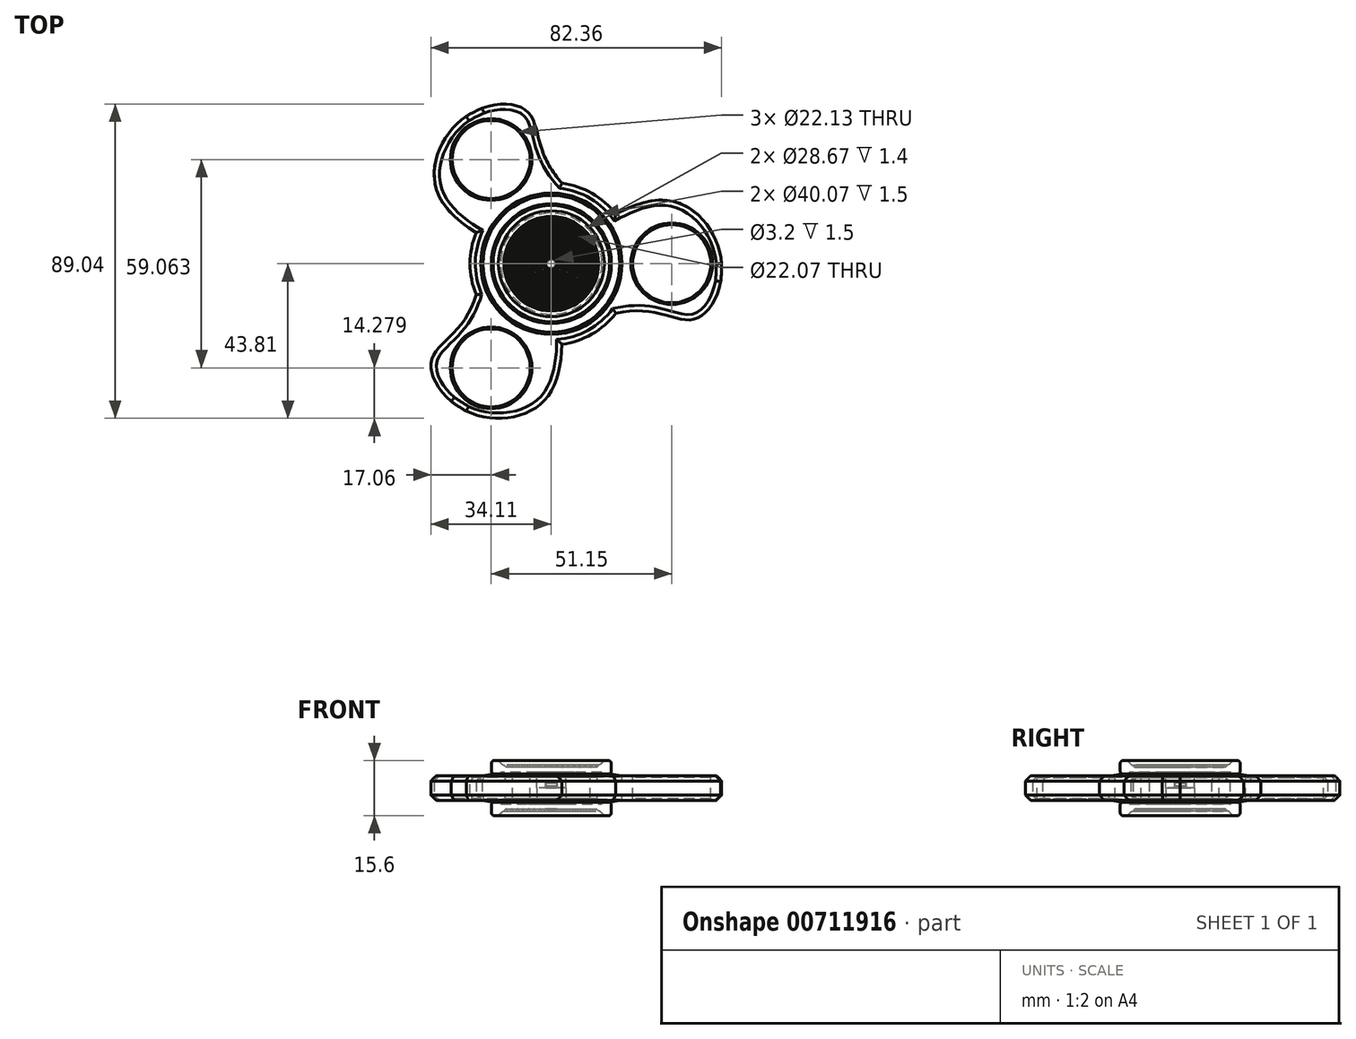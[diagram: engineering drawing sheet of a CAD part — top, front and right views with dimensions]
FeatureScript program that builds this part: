
annotation { "Feature Type Name" : "Feature", "Feature Type Description" : "" }
export const myFeature = defineFeature(function(context is Context, id is Id, definition is map)
    precondition{}
    {
        {
            var Q0;
            Q0=qCreatedBy(makeId("Front.planeOp"),FACE);
            var sketch = newSketch(context, id + "F0", { "sketchPlane" : qUnion([Q0])});
            skLineSegment(sketch, "E0", {"start": v(0, 0) * mm, "end": v(0, 3.5) * mm});
            skLineSegment(sketch, "E1", {"start": v(0, 3.5) * mm, "end": v(13.04, 3.5) * mm});
            skLineSegment(sketch, "E2", {"start": v(13.04, 3.5) * mm, "end": v(13.04, 2) * mm});
            skLineSegment(sketch, "E3", {"start": v(13.04, 2) * mm, "end": v(20.04, 2) * mm});
            skLineSegment(sketch, "E4", {"start": v(20.04, 2) * mm, "end": v(20.04, 3.5) * mm});
            skLineSegment(sketch, "E5", {"start": v(20.04, 3.5) * mm, "end": v(23.04, 3.5) * mm});
            skLineSegment(sketch, "E6", {"start": v(23.04, 3.5) * mm, "end": v(23.04, 0) * mm});
            skLineSegment(sketch, "E7", {"start": v(23.04, 0) * mm, "end": v(45.16, 0) * mm});
            skLineSegment(sketch, "E8", {"start": v(45.16, 0) * mm, "end": v(45.16, 3.5) * mm});
            skLineSegment(sketch, "E9", {"start": v(45.16, 3.5) * mm, "end": v(47.16, 3.5) * mm});
            skLineSegment(sketch, "E10", {"start": v(47.16, 3.5) * mm, "end": v(48.16, 1.5) * mm});
            skLineSegment(sketch, "E11", {"start": v(48.16, 1.5) * mm, "end": v(48.16, 0) * mm});
            skLineSegment(sketch, "E12", {"start": v(48.16, 0) * mm, "end": v(45.16, 0) * mm});
            skLineSegment(sketch, "E13", {"start": v(23.04, 0) * mm, "end": v(11.04, 0) * mm});
            skLineSegment(sketch, "E14", {"start": v(11.04, 0) * mm, "end": v(11.04, 3.5) * mm});
            skLineSegment(sketch, "E15", {"start": v(23.04, 3.5) * mm, "end": v(45.16, 3.5) * mm});
            skLineSegment(sketch, "E16", {"start": v(34.1, 0) * mm, "end": v(34.1, 3.5) * mm});
            skLineSegment(sketch, "E17", {"start": v(17, 4.5) * mm, "end": v(17, 6.5) * mm});
            skLineSegment(sketch, "E18", {"start": v(17, 6.5) * mm, "end": v(0, 6.5) * mm});
            skLineSegment(sketch, "E19", {"start": v(0, 6.5) * mm, "end": v(0, 0) * mm});
            skLineSegment(sketch, "E20", {"start": v(0, 0) * mm, "end": v(4.08, 0) * mm});
            skLineSegment(sketch, "E21", {"start": v(4.08, 0) * mm, "end": v(4.08, 3.5) * mm});
            skLineSegment(sketch, "E22", {"start": v(4.08, 3.5) * mm, "end": v(6.58, 3.5) * mm});
            skLineSegment(sketch, "E23", {"start": v(6.58, 3.5) * mm, "end": v(6.58, 4.5) * mm});
            skLineSegment(sketch, "E24", {"start": v(6.58, 4.5) * mm, "end": v(17, 4.5) * mm});
            skLineSegment(sketch, "E25", {"start": v(17, 6.5) * mm, "end": v(17, 7.8) * mm});
            skLineSegment(sketch, "E26", {"start": v(17, 7.8) * mm, "end": v(15, 7.8) * mm});
            skLineSegment(sketch, "E27", {"start": v(15, 7.8) * mm, "end": v(13.7, 6.5) * mm});
            skLineSegment(sketch, "E28.MirrorCS", {"start": v(13.04, -3.5) * mm, "end": v(13.04, -2) * mm});
            skLineSegment(sketch, "E29.MirrorCS", {"start": v(4.08, -3.5) * mm, "end": v(6.58, -3.5) * mm});
            skLineSegment(sketch, "E30.MirrorCS", {"start": v(20.04, -3.5) * mm, "end": v(23.04, -3.5) * mm});
            skLineSegment(sketch, "E31.MirrorCS", {"start": v(20.04, -2) * mm, "end": v(20.04, -3.5) * mm});
            skLineSegment(sketch, "E32.MirrorCS", {"start": v(47.16, -3.5) * mm, "end": v(48.16, -1.5) * mm});
            skLineSegment(sketch, "E33.MirrorCS", {"start": v(45.16, -3.5) * mm, "end": v(47.16, -3.5) * mm});
            skLineSegment(sketch, "E34.MirrorCS", {"start": v(0, -3.5) * mm, "end": v(13.04, -3.5) * mm});
            skLineSegment(sketch, "E35.MirrorCS", {"start": v(23.04, -3.5) * mm, "end": v(45.16, -3.5) * mm});
            skLineSegment(sketch, "E36.MirrorCS", {"start": v(13.04, -2) * mm, "end": v(20.04, -2) * mm});
            skLineSegment(sketch, "E37.MirrorCS", {"start": v(48.16, -1.5) * mm, "end": v(48.16, 0) * mm});
            skLineSegment(sketch, "E38.MirrorCS", {"start": v(45.16, 0) * mm, "end": v(45.16, -3.5) * mm});
            skLineSegment(sketch, "E39.MirrorCS", {"start": v(34.1, 0) * mm, "end": v(34.1, -3.5) * mm});
            skLineSegment(sketch, "E40.MirrorCS", {"start": v(23.04, -3.5) * mm, "end": v(23.04, 0) * mm});
            skLineSegment(sketch, "E41.MirrorCS", {"start": v(11.04, 0) * mm, "end": v(11.04, -3.5) * mm});
            skLineSegment(sketch, "E42.MirrorCS", {"start": v(4.08, 0) * mm, "end": v(4.08, -3.5) * mm});
            skLineSegment(sketch, "E43", {"start": v(1.6, 0) * mm, "end": v(1.6, 2) * mm});
            skLineSegment(sketch, "E44", {"start": v(1.6, 2) * mm, "end": v(0, 2) * mm});
            skLineSegment(sketch, "E45", {"start": v(14.34, 4.5) * mm, "end": v(14.34, 3.1) * mm});
            skLineSegment(sketch, "E46", {"start": v(14.34, 3.1) * mm, "end": v(19.38, 3.1) * mm});
            skLineSegment(sketch, "E47", {"start": v(19.38, 3.1) * mm, "end": v(19.38, 3.5) * mm});
            skLineSegment(sketch, "E48", {"start": v(19.38, 3.5) * mm, "end": v(16.5, 4) * mm});
            skLineSegment(sketch, "E49", {"start": v(16.5, 4) * mm, "end": v(17, 4.5) * mm});
            skLineSegment(sketch, "E50.MirrorCS", {"start": v(17, -4.5) * mm, "end": v(17, -6.5) * mm});
            skLineSegment(sketch, "E51.MirrorCS", {"start": v(17, -7.8) * mm, "end": v(15, -7.8) * mm});
            skLineSegment(sketch, "E52.MirrorCS", {"start": v(17, -6.5) * mm, "end": v(17, -7.8) * mm});
            skLineSegment(sketch, "E53.MirrorCS", {"start": v(17, -6.5) * mm, "end": v(0, -6.5) * mm});
            skLineSegment(sketch, "E54.MirrorCS", {"start": v(6.58, -4.5) * mm, "end": v(17, -4.5) * mm});
            skLineSegment(sketch, "E55.MirrorCS", {"start": v(15, -7.8) * mm, "end": v(13.7, -6.5) * mm});
            skLineSegment(sketch, "E56.MirrorCS", {"start": v(14.34, -3.1) * mm, "end": v(19.39, -3.1) * mm});
            skLineSegment(sketch, "E57.MirrorCS", {"start": v(19.39, -3.5) * mm, "end": v(16.5, -4) * mm});
            skLineSegment(sketch, "E58.MirrorCS", {"start": v(16.5, -4) * mm, "end": v(17, -4.5) * mm});
            skLineSegment(sketch, "E59.MirrorCS", {"start": v(14.34, -4.5) * mm, "end": v(14.34, -3.1) * mm});
            skLineSegment(sketch, "E60.MirrorCS", {"start": v(6.58, -3.5) * mm, "end": v(6.58, -4.5) * mm});
            skLineSegment(sketch, "E61.MirrorCS", {"start": v(0, -6.5) * mm, "end": v(0, 0) * mm});
            skLineSegment(sketch, "E62.MirrorCS", {"start": v(19.38, -3.1) * mm, "end": v(19.38, -3.5) * mm});
            skLineSegment(sketch, "E63", {"start": v(1, 6.5) * mm, "end": v(1.6, 5.9) * mm});
            skLineSegment(sketch, "E64", {"start": v(1.6, 5.9) * mm, "end": v(2.2, 6.5) * mm});
            skLineSegment(sketch, "E65.1.0.0", {"start": v(3.2, 5.9) * mm, "end": v(3.8, 6.5) * mm});
            skLineSegment(sketch, "E65.1.0.1", {"start": v(2.6, 6.5) * mm, "end": v(3.2, 5.9) * mm});
            skLineSegment(sketch, "E65.2.0.0", {"start": v(4.8, 5.9) * mm, "end": v(5.4, 6.5) * mm});
            skLineSegment(sketch, "E65.2.0.1", {"start": v(4.2, 6.5) * mm, "end": v(4.8, 5.9) * mm});
            skLineSegment(sketch, "E65.3.0.0", {"start": v(6.4, 5.9) * mm, "end": v(7, 6.5) * mm});
            skLineSegment(sketch, "E65.3.0.1", {"start": v(5.8, 6.5) * mm, "end": v(6.4, 5.9) * mm});
            skLineSegment(sketch, "E65.4.0.0", {"start": v(8, 5.9) * mm, "end": v(8.6, 6.5) * mm});
            skLineSegment(sketch, "E65.4.0.1", {"start": v(7.4, 6.5) * mm, "end": v(8, 5.9) * mm});
            skLineSegment(sketch, "E65.5.0.0", {"start": v(9.6, 5.9) * mm, "end": v(10.2, 6.5) * mm});
            skLineSegment(sketch, "E65.5.0.1", {"start": v(9, 6.5) * mm, "end": v(9.6, 5.9) * mm});
            skLineSegment(sketch, "E65.6.0.0", {"start": v(11.2, 5.9) * mm, "end": v(11.8, 6.5) * mm});
            skLineSegment(sketch, "E65.6.0.1", {"start": v(10.6, 6.5) * mm, "end": v(11.2, 5.9) * mm});
            skLineSegment(sketch, "E65.7.0.0", {"start": v(12.8, 5.9) * mm, "end": v(13.4, 6.5) * mm});
            skLineSegment(sketch, "E65.7.0.1", {"start": v(12.2, 6.5) * mm, "end": v(12.8, 5.9) * mm});
            skLineSegment(sketch, "E65.direction1", {"start": v(1.6, 5.9) * mm, "end": v(3.2, 5.9) * mm, "construction": true});
            skLineSegment(sketch, "E66.MirrorCS", {"start": v(1, -6.5) * mm, "end": v(1.6, -5.9) * mm});
            skLineSegment(sketch, "E67.MirrorCS", {"start": v(2.6, -6.5) * mm, "end": v(3.2, -5.9) * mm});
            skLineSegment(sketch, "E68.MirrorCS", {"start": v(1.6, -5.9) * mm, "end": v(2.2, -6.5) * mm});
            skLineSegment(sketch, "E69.MirrorCS", {"start": v(8, -5.9) * mm, "end": v(8.6, -6.5) * mm});
            skLineSegment(sketch, "E70.MirrorCS", {"start": v(9.6, -5.9) * mm, "end": v(10.2, -6.5) * mm});
            skLineSegment(sketch, "E71.MirrorCS", {"start": v(7.4, -6.5) * mm, "end": v(8, -5.9) * mm});
            skLineSegment(sketch, "E72.MirrorCS", {"start": v(10.6, -6.5) * mm, "end": v(11.2, -5.9) * mm});
            skLineSegment(sketch, "E73.MirrorCS", {"start": v(12.2, -6.5) * mm, "end": v(12.8, -5.9) * mm});
            skLineSegment(sketch, "E74.MirrorCS", {"start": v(6.4, -5.9) * mm, "end": v(7, -6.5) * mm});
            skLineSegment(sketch, "E75.MirrorCS", {"start": v(1.6, -5.9) * mm, "end": v(3.2, -5.9) * mm, "construction": true});
            skLineSegment(sketch, "E76.MirrorCS", {"start": v(11.2, -5.9) * mm, "end": v(11.8, -6.5) * mm});
            skLineSegment(sketch, "E77.MirrorCS", {"start": v(3.2, -5.9) * mm, "end": v(3.8, -6.5) * mm});
            skLineSegment(sketch, "E78.MirrorCS", {"start": v(12.8, -5.9) * mm, "end": v(13.4, -6.5) * mm});
            skLineSegment(sketch, "E79.MirrorCS", {"start": v(9, -6.5) * mm, "end": v(9.6, -5.9) * mm});
            skLineSegment(sketch, "E80.MirrorCS", {"start": v(4.8, -5.9) * mm, "end": v(5.4, -6.5) * mm});
            skLineSegment(sketch, "E81.MirrorCS", {"start": v(5.8, -6.5) * mm, "end": v(6.4, -5.9) * mm});
            skLineSegment(sketch, "E82.MirrorCS", {"start": v(4.2, -6.5) * mm, "end": v(4.8, -5.9) * mm});
            skSolve(sketch);
        }
        {
            var Q0;
            {var subQ1=sQuery(id+"F0.wireOp",EDGE,"E2");Q0=makeQuery(id+"F0.imprint","IMPRINT",FACE,{"disambiguationData":[TD([[makeQuery(id+"F0.imprint","IMPRINT",EDGE,{"derivedFrom":subQ1}),-1.0]])]});}
            var Q1;
            Q1=makeQuery(id+"F0.imprint","IMPRINT",FACE,{"disambiguationData":[TD([[makeQuery(id+"F0.imprint","IMPRINT",EDGE,{"derivedFrom":sQuery(id+"F0.wireOp",EDGE,"E13")}),1.0]])]});
            var Q2;
            {var subQ0=sQuery(id+"F0.wireOp",EDGE,"E6");Q2=makeQuery(id+"F0.imprint","IMPRINT",FACE,{"disambiguationData":[TD([[makeQuery(id+"F0.imprint","IMPRINT",EDGE,{"derivedFrom":subQ0}),1.0]])]});}
            var Q3;
            {var subQ2=sQuery(id+"F0.wireOp",EDGE,"E39.MirrorCS");Q3=makeQuery(id+"F0.imprint","IMPRINT",FACE,{"disambiguationData":[TD([[makeQuery(id+"F0.imprint","IMPRINT",EDGE,{"derivedFrom":subQ2}),-1.0]])]});}
            var Q4;
            {var subQ0=sQuery(id+"F0.wireOp",EDGE,"E8");Q4=makeQuery(id+"F0.imprint","IMPRINT",FACE,{"disambiguationData":[TD([[makeQuery(id+"F0.imprint","IMPRINT",EDGE,{"derivedFrom":subQ0}),1.0]])]});}
            var Q5;
            {var subQ0=sQuery(id+"F0.wireOp",EDGE,"E38.MirrorCS");Q5=makeQuery(id+"F0.imprint","IMPRINT",FACE,{"disambiguationData":[TD([[makeQuery(id+"F0.imprint","IMPRINT",EDGE,{"derivedFrom":subQ0}),-1.0]])]});}
            var Q6;
            Q6=makeQuery(id+"F0.imprint","IMPRINT",FACE,{"disambiguationData":[TD([[makeQuery(id+"F0.imprint","IMPRINT",EDGE,{"derivedFrom":sQuery(id+"F0.wireOp",EDGE,"E8")}),-1.0]])]});
            var Q7;
            Q7=makeQuery(id+"F0.imprint","IMPRINT",FACE,{"disambiguationData":[TD([[makeQuery(id+"F0.imprint","IMPRINT",EDGE,{"derivedFrom":sQuery(id+"F0.wireOp",EDGE,"E12")}),1.0]])]});
            var Q8;
            Q8=sQuery(id+"F0.wireOp",EDGE,"E19");
            revolve(context, id + "F1", {"surfaceOperationType" : NewSurfaceOperationType.NEW, "entities" : qUnion([Q0, Q1, Q2, Q3, Q4, Q5, Q6, Q7]), "axis" : qUnion([Q8]), "revolveType" : RevolveType.FULL});
        }
        {
            var Q0;
            {var subQ0=sQuery(id+"F0.wireOp",EDGE,"E8");Q0=makeQuery(id+"F0.imprint","IMPRINT",FACE,{"disambiguationData":[TD([[makeQuery(id+"F0.imprint","IMPRINT",EDGE,{"derivedFrom":subQ0}),1.0]])]});}
            var Q1;
            {var subQ0=sQuery(id+"F0.wireOp",EDGE,"E38.MirrorCS");Q1=makeQuery(id+"F0.imprint","IMPRINT",FACE,{"disambiguationData":[TD([[makeQuery(id+"F0.imprint","IMPRINT",EDGE,{"derivedFrom":subQ0}),-1.0]])]});}
            var Q2;
            Q2=sQuery(id+"F0.wireOp",EDGE,"E39.MirrorCS");
            revolve(context, id + "F2", {"surfaceOperationType" : NewSurfaceOperationType.NEW, "entities" : qUnion([Q0, Q1]), "axis" : qUnion([Q2]), "revolveType" : RevolveType.FULL});
        }
        {
            var Q0;
            Q0=makeQuery(id+"F0.imprint","IMPRINT",FACE,{"disambiguationData":[TD([[makeQuery(id+"F0.imprint","IMPRINT",EDGE,{"derivedFrom":sQuery(id+"F0.wireOp",EDGE,"KGeZFjar-oYJH-GqHQ-ATJc-c8EllFN0LwBf")}),1.0]])]});
            var Q1;
            {var subQ0=sQuery(id+"F0.wireOp",EDGE,"E21");Q1=makeQuery(id+"F0.imprint","IMPRINT",FACE,{"disambiguationData":[TD([[makeQuery(id+"F0.imprint","IMPRINT",EDGE,{"derivedFrom":subQ0}),1.0]])]});}
            var Q2;
            {var subQ0=sQuery(id+"F0.wireOp",EDGE,"E25");Q2=makeQuery(id+"F0.imprint","IMPRINT",FACE,{"disambiguationData":[TD([[makeQuery(id+"F0.imprint","IMPRINT",EDGE,{"derivedFrom":subQ0}),1.0]])]});}
            var Q3;
            {var subQ1=sQuery(id+"F0.wireOp",EDGE,"E17");Q3=makeQuery(id+"F0.imprint","IMPRINT",FACE,{"disambiguationData":[TD([[makeQuery(id+"F0.imprint","IMPRINT",EDGE,{"derivedFrom":subQ1}),1.0]])]});}
            var Q4;
            {var subQ0=sQuery(id+"F0.wireOp",EDGE,"E45");Q4=makeQuery(id+"F0.imprint","IMPRINT",FACE,{"disambiguationData":[TD([[makeQuery(id+"F0.imprint","IMPRINT",EDGE,{"derivedFrom":subQ0}),1.0]])]});}
            var Q5;
            Q5=makeQuery(id+"F0.imprint","IMPRINT",FACE,{"disambiguationData":[TD([[makeQuery(id+"F0.imprint","IMPRINT",EDGE,{"derivedFrom":sQuery(id+"F0.wireOp",EDGE,"vZCheLl1-PAfG-MPR2-0KO7-rnN0XizPisMo.bottom")}),-1.0]])]});
            var Q6;
            Q6=sQuery(id+"F0.wireOp",EDGE,"E19");
            revolve(context, id + "F3", {"surfaceOperationType" : NewSurfaceOperationType.NEW, "entities" : qUnion([Q0, Q1, Q2, Q3, Q4, Q5]), "axis" : qUnion([Q6]), "revolveType" : RevolveType.FULL});
        }
        {
            var Q0;
            {var subQ0=sQuery(id+"F0.wireOp",EDGE,"E42.MirrorCS");Q0=makeQuery(id+"F0.imprint","IMPRINT",FACE,{"disambiguationData":[TD([[makeQuery(id+"F0.imprint","IMPRINT",EDGE,{"derivedFrom":subQ0}),-1.0]])]});}
            var Q1;
            {var subQ9=sQuery(id+"F0.wireOp",EDGE,"E50.MirrorCS");Q1=makeQuery(id+"F0.imprint","IMPRINT",FACE,{"disambiguationData":[TD([[makeQuery(id+"F0.imprint","IMPRINT",EDGE,{"derivedFrom":subQ9}),-1.0]])]});}
            var Q2;
            {var subQ0=sQuery(id+"F0.wireOp",EDGE,"3c67924d-497e-40e4-b348-fd03371842f01.MirrorCS");Q2=makeQuery(id+"F0.imprint","IMPRINT",FACE,{"disambiguationData":[TD([[makeQuery(id+"F0.imprint","IMPRINT",EDGE,{"derivedFrom":subQ0}),1.0]])]});}
            var Q3;
            Q3=makeQuery(id+"F0.imprint","IMPRINT",FACE,{"disambiguationData":[TD([[makeQuery(id+"F0.imprint","IMPRINT",EDGE,{"derivedFrom":sQuery(id+"F0.wireOp",EDGE,"E56.MirrorCS")}),-1.0]])]});
            var Q4;
            Q4=makeQuery(id+"F0.imprint","IMPRINT",FACE,{"disambiguationData":[TD([[makeQuery(id+"F0.imprint","IMPRINT",EDGE,{"derivedFrom":sQuery(id+"F0.wireOp",EDGE,"E51.MirrorCS")}),-1.0]])]});
            var Q5;
            {var subQ4=sQuery(id+"F0.wireOp",EDGE,"E43");Q5=makeQuery(id+"F0.imprint","IMPRINT",FACE,{"disambiguationData":[TD([[makeQuery(id+"F0.imprint","IMPRINT",EDGE,{"derivedFrom":subQ4}),1.0]])]});}
            var Q6;
            {var subQ3=sQuery(id+"F0.wireOp",EDGE,"E44");Q6=makeQuery(id+"F0.imprint","IMPRINT",FACE,{"disambiguationData":[TD([[makeQuery(id+"F0.imprint","IMPRINT",EDGE,{"derivedFrom":subQ3}),1.0]])]});}
            var Q7;
            Q7=sQuery(id+"F0.wireOp",EDGE,"E61.MirrorCS");
            revolve(context, id + "F4", {"surfaceOperationType" : NewSurfaceOperationType.NEW, "entities" : qUnion([Q0, Q1, Q2, Q3, Q4, Q5, Q6]), "axis" : qUnion([Q7]), "revolveType" : RevolveType.FULL});
        }
        {
            var Q0;
            Q0=makeQuery(id+"F2.opRevolve","SWEPT_BODY",BODY,{"disambiguationData":[OSD([sQuery(id+"F0.wireOp",EDGE,"E8"),sQuery(id+"F0.wireOp",EDGE,"E15"),sQuery(id+"F0.wireOp",EDGE,"E16"),sQuery(id+"F0.wireOp",EDGE,"E35.MirrorCS"),sQuery(id+"F0.wireOp",EDGE,"E38.MirrorCS"),sQuery(id+"F0.wireOp",EDGE,"E39.MirrorCS")])]});
            var Q1;
            Q1=makeQuery(id+"F1.opRevolve","SWEPT_EDGE",EDGE,{"disambiguationData":[OSD([sQuery(id+"F0.wireOp",EDGE,"E34.MirrorCS"),sQuery(id+"F0.wireOp",EDGE,"E41.MirrorCS")])]});
            circularPattern(context, id + "F5", {"entities" : qUnion([Q0]), "axis" : qUnion([Q1]), "angle" : 360 * degree, "instanceCount" : 3, "equalSpace" : true});
        }
        {
            var Q0;
            Q0=qCreatedBy(makeId("Top.planeOp"),FACE);
            var sketch = newSketch(context, id + "F6", { "sketchPlane" : qUnion([Q0])});
            skCircle(sketch, "E83", {"center": v(0, 0) * mm, "radius": 48.25 * mm});
            skFitSpline(sketch, "E84", {"points": [v(0, -25) * mm, v(27.25, -13.5) * mm, v(41.25, -15.5) * mm, v(48.25, 0) * mm, v(34, 17.78) * mm, v(0, 0) * mm], "startDerivative": vector(107.2, 120.6) * mm, "endDerivative": vector(-125.88, -120.18) * mm});
            skCircle(sketch, "E85", {"center": v(0, 0) * mm, "radius": 22.05 * mm});
            skSolve(sketch);
        }
        {
            var Q0;
            {var subQ0=sQuery(id+"F6.wireOp",EDGE,"E84");var subQ1=sQuery(id+"F6.wireOp",EDGE,"E83");var subQ2=makeQuery(id+"F6.imprint","INTERSECT",VERTEX,{"disambiguationData":[OD(0.0)],"derivedFrom":[subQ1,subQ0]});Q0=makeQuery(id+"F6.imprint","IMPRINT",FACE,{"disambiguationData":[TD([[makeQuery(id+"F6.imprint","IMPRINT",EDGE,{"disambiguationData":[TD([[subQ2,-1.0]])],"derivedFrom":subQ1}),1.0]])]});}
            extrude(context, id + "F7", {"entities" : qUnion([Q0]), "depth" : 3.5 * mm, "offsetDistance" : 25 * mm, "hasSecondDirection" : true, "secondDirectionOppositeDirection" : true, "secondDirectionDepth" : 3.5 * mm});
        }
        {
            var Q0;
            Q0=makeQuery(id+"F7.opExtrude","SWEPT_BODY",BODY,{"disambiguationData":[OSD([sQuery(id+"F6.wireOp",EDGE,"E83"),sQuery(id+"F6.wireOp",EDGE,"E84"),sQuery(id+"F6.wireOp",EDGE,"E85")])]});
            var Q1;
            Q1=makeQuery(id+"F1.opRevolve","SWEPT_FACE",FACE,{"disambiguationData":[OSD([sQuery(id+"F0.wireOp",EDGE,"E14"),sQuery(id+"F0.wireOp",EDGE,"E41.MirrorCS")])]});
            circularPattern(context, id + "F8", {"entities" : qUnion([Q0]), "axis" : qUnion([Q1]), "angle" : 360 * degree, "instanceCount" : 3, "equalSpace" : true});
        }
        {
            var Q0;
            {var subQ1=sQuery(id+"F0.wireOp",EDGE,"E2");Q0=makeQuery(id+"F0.imprint","IMPRINT",FACE,{"disambiguationData":[TD([[makeQuery(id+"F0.imprint","IMPRINT",EDGE,{"derivedFrom":subQ1}),-1.0]])]});}
            var Q1;
            Q1=makeQuery(id+"F0.imprint","IMPRINT",FACE,{"disambiguationData":[TD([[makeQuery(id+"F0.imprint","IMPRINT",EDGE,{"derivedFrom":sQuery(id+"F0.wireOp",EDGE,"E13")}),1.0]])]});
            var Q2;
            Q2=sQuery(id+"F0.wireOp",EDGE,"E19");
            revolve(context, id + "F9", {"surfaceOperationType" : NewSurfaceOperationType.NEW, "entities" : qUnion([Q0, Q1]), "axis" : qUnion([Q2]), "revolveType" : RevolveType.FULL});
        }
        {
            var Q0;
            Q0=makeQuery(id+"F8.opPattern","COPY",BODY,{"derivedFrom":makeQuery(id+"F7.opExtrude","SWEPT_BODY",BODY,{"disambiguationData":[OSD([sQuery(id+"F6.wireOp",EDGE,"E83"),sQuery(id+"F6.wireOp",EDGE,"E84"),sQuery(id+"F6.wireOp",EDGE,"E85")])]}),"instanceName":"2"});
            var Q1;
            Q1=makeQuery(id+"F8.opPattern","COPY",BODY,{"derivedFrom":makeQuery(id+"F7.opExtrude","SWEPT_BODY",BODY,{"disambiguationData":[OSD([sQuery(id+"F6.wireOp",EDGE,"E83"),sQuery(id+"F6.wireOp",EDGE,"E84"),sQuery(id+"F6.wireOp",EDGE,"E85")])]}),"instanceName":"1"});
            var Q2;
            Q2=makeQuery(id+"F7.opExtrude","SWEPT_BODY",BODY,{"disambiguationData":[OSD([sQuery(id+"F6.wireOp",EDGE,"E83"),sQuery(id+"F6.wireOp",EDGE,"E84"),sQuery(id+"F6.wireOp",EDGE,"E85")])]});
            var Q3;
            Q3=makeQuery(id+"F9.opRevolve","SWEPT_BODY",BODY,{"disambiguationData":[OSD([sQuery(id+"F0.wireOp",EDGE,"E1"),sQuery(id+"F0.wireOp",EDGE,"E2"),sQuery(id+"F0.wireOp",EDGE,"E3"),sQuery(id+"F0.wireOp",EDGE,"E4"),sQuery(id+"F0.wireOp",EDGE,"E5"),sQuery(id+"F0.wireOp",EDGE,"E6"),sQuery(id+"F0.wireOp",EDGE,"E19"),sQuery(id+"F0.wireOp",EDGE,"E22"),sQuery(id+"F0.wireOp",EDGE,"E28.MirrorCS"),sQuery(id+"F0.wireOp",EDGE,"E30.MirrorCS"),sQuery(id+"F0.wireOp",EDGE,"E31.MirrorCS"),sQuery(id+"F0.wireOp",EDGE,"E34.MirrorCS"),sQuery(id+"F0.wireOp",EDGE,"E36.MirrorCS"),sQuery(id+"F0.wireOp",EDGE,"E40.MirrorCS"),sQuery(id+"F0.wireOp",EDGE,"05ecb766-ba4e-4d32-9f54-2b1253087cd20.MirrorCS")])]});
            booleanBodies(context, id + "F10", {"operationType" : BooleanOperationType.UNION, "tools" : qUnion([Q0, Q1, Q2, Q3])});
        }
        {
            var Q0;
            Q0=makeQuery(id+"F1.opRevolve","SWEPT_BODY",BODY,{"disambiguationData":[OSD([sQuery(id+"F0.wireOp",EDGE,"E1"),sQuery(id+"F0.wireOp",EDGE,"E2"),sQuery(id+"F0.wireOp",EDGE,"E3"),sQuery(id+"F0.wireOp",EDGE,"E4"),sQuery(id+"F0.wireOp",EDGE,"E5"),sQuery(id+"F0.wireOp",EDGE,"E9"),sQuery(id+"F0.wireOp",EDGE,"E10"),sQuery(id+"F0.wireOp",EDGE,"E11"),sQuery(id+"F0.wireOp",EDGE,"E14"),sQuery(id+"F0.wireOp",EDGE,"E15"),sQuery(id+"F0.wireOp",EDGE,"E28.MirrorCS"),sQuery(id+"F0.wireOp",EDGE,"E30.MirrorCS"),sQuery(id+"F0.wireOp",EDGE,"E31.MirrorCS"),sQuery(id+"F0.wireOp",EDGE,"E32.MirrorCS"),sQuery(id+"F0.wireOp",EDGE,"E33.MirrorCS"),sQuery(id+"F0.wireOp",EDGE,"E34.MirrorCS"),sQuery(id+"F0.wireOp",EDGE,"E35.MirrorCS"),sQuery(id+"F0.wireOp",EDGE,"E36.MirrorCS"),sQuery(id+"F0.wireOp",EDGE,"E37.MirrorCS"),sQuery(id+"F0.wireOp",EDGE,"E41.MirrorCS")])]});
            deleteBodies(context, id + "F11", {"entities" : qUnion([Q0])});
        }
        {
            var Q0;
            Q0=makeQuery(id+"F5.opPattern","COPY",BODY,{"derivedFrom":makeQuery(id+"F2.opRevolve","SWEPT_BODY",BODY,{"disambiguationData":[OSD([sQuery(id+"F0.wireOp",EDGE,"E8"),sQuery(id+"F0.wireOp",EDGE,"E15"),sQuery(id+"F0.wireOp",EDGE,"E16"),sQuery(id+"F0.wireOp",EDGE,"E35.MirrorCS"),sQuery(id+"F0.wireOp",EDGE,"E38.MirrorCS"),sQuery(id+"F0.wireOp",EDGE,"E39.MirrorCS")])]}),"instanceName":"2"});
            var Q1;
            Q1=makeQuery(id+"F5.opPattern","COPY",BODY,{"derivedFrom":makeQuery(id+"F2.opRevolve","SWEPT_BODY",BODY,{"disambiguationData":[OSD([sQuery(id+"F0.wireOp",EDGE,"E8"),sQuery(id+"F0.wireOp",EDGE,"E15"),sQuery(id+"F0.wireOp",EDGE,"E16"),sQuery(id+"F0.wireOp",EDGE,"E35.MirrorCS"),sQuery(id+"F0.wireOp",EDGE,"E38.MirrorCS"),sQuery(id+"F0.wireOp",EDGE,"E39.MirrorCS")])]}),"instanceName":"1"});
            var Q2;
            Q2=makeQuery(id+"F2.opRevolve","SWEPT_BODY",BODY,{"disambiguationData":[OSD([sQuery(id+"F0.wireOp",EDGE,"E8"),sQuery(id+"F0.wireOp",EDGE,"E15"),sQuery(id+"F0.wireOp",EDGE,"E16"),sQuery(id+"F0.wireOp",EDGE,"E35.MirrorCS"),sQuery(id+"F0.wireOp",EDGE,"E38.MirrorCS"),sQuery(id+"F0.wireOp",EDGE,"E39.MirrorCS")])]});
            var Q3;
            Q3=makeQuery(id+"F8.opPattern","COPY",BODY,{"derivedFrom":makeQuery(id+"F7.opExtrude","SWEPT_BODY",BODY,{"disambiguationData":[OSD([sQuery(id+"F6.wireOp",EDGE,"E83"),sQuery(id+"F6.wireOp",EDGE,"E84"),sQuery(id+"F6.wireOp",EDGE,"E85")])]}),"instanceName":"2"});
            booleanBodies(context, id + "F12", {"operationType" : BooleanOperationType.SUBTRACTION, "tools" : qUnion([Q0, Q1, Q2]), "targets" : qUnion([Q3])});
        }
        {
            var Q0;
            Q0=makeQuery(id+"F9.opRevolve","SWEPT_EDGE",EDGE,{"disambiguationData":[OSD([sQuery(id+"F0.wireOp",EDGE,"E28.MirrorCS"),sQuery(id+"F0.wireOp",EDGE,"E34.MirrorCS")])]});
            var Q1;
            Q1=makeQuery(id+"F9.opRevolve","SWEPT_EDGE",EDGE,{"disambiguationData":[OSD([sQuery(id+"F0.wireOp",EDGE,"E34.MirrorCS"),sQuery(id+"F0.wireOp",EDGE,"E41.MirrorCS")])]});
            var Q2;
            Q2=makeQuery(id+"F12.opBoolean","COPY",FACE,{"derivedFrom":makeQuery(id+"F5.opPattern","COPY",FACE,{"derivedFrom":makeQuery(id+"F2.opRevolve","SWEPT_FACE",FACE,{"disambiguationData":[OSD([sQuery(id+"F0.wireOp",EDGE,"E8"),sQuery(id+"F0.wireOp",EDGE,"E38.MirrorCS")])]}),"instanceName":"1"})});
            var Q3;
            Q3=makeQuery(id+"F12.opBoolean","COPY",FACE,{"derivedFrom":makeQuery(id+"F5.opPattern","COPY",FACE,{"derivedFrom":makeQuery(id+"F2.opRevolve","SWEPT_FACE",FACE,{"disambiguationData":[OSD([sQuery(id+"F0.wireOp",EDGE,"E8"),sQuery(id+"F0.wireOp",EDGE,"E38.MirrorCS")])]}),"instanceName":"2"})});
            var Q4;
            Q4=makeQuery(id+"F12.opBoolean","COPY",FACE,{"derivedFrom":makeQuery(id+"F2.opRevolve","SWEPT_FACE",FACE,{"disambiguationData":[OSD([sQuery(id+"F0.wireOp",EDGE,"E8"),sQuery(id+"F0.wireOp",EDGE,"E38.MirrorCS")])]})});
            var Q5;
            Q5=makeQuery(id+"F9.opRevolve","SWEPT_FACE",FACE,{"disambiguationData":[OSD([sQuery(id+"F0.wireOp",EDGE,"E1")])]});
            var Q6;
            Q6=makeQuery(id+"F4.opRevolve","SWEPT_EDGE",EDGE,{"disambiguationData":[OSD([sQuery(id+"F0.wireOp",EDGE,"E43"),sQuery(id+"F0.wireOp",EDGE,"E44")])]});
            var Q7;
            Q7=makeQuery(id+"F4.opRevolve","SWEPT_EDGE",EDGE,{"disambiguationData":[OSD([sQuery(id+"F0.wireOp",EDGE,"b50aee2d-b4f1-476f-93b3-e66e5736d9cd34.MirrorCS"),sQuery(id+"F0.wireOp",EDGE,"b50aee2d-b4f1-476f-93b3-e66e5736d9cd41.MirrorCS")])]});
            var Q8;
            Q8=makeQuery(id+"F4.opRevolve","SWEPT_EDGE",EDGE,{"disambiguationData":[OSD([sQuery(id+"F0.wireOp",EDGE,"b50aee2d-b4f1-476f-93b3-e66e5736d9cd12.MirrorCS"),sQuery(id+"F0.wireOp",EDGE,"b50aee2d-b4f1-476f-93b3-e66e5736d9cd41.MirrorCS")])]});
            var Q9;
            Q9=makeQuery(id+"F3.opRevolve","SWEPT_EDGE",EDGE,{"disambiguationData":[OSD([sQuery(id+"F0.wireOp",EDGE,"E20"),sQuery(id+"F0.wireOp",EDGE,"E43")])]});
            var Q10;
            Q10=makeQuery(id+"F3.opRevolve","SWEPT_EDGE",EDGE,{"disambiguationData":[OSD([sQuery(id+"F0.wireOp",EDGE,"KGeZFjar-oYJH-GqHQ-ATJc-c8EllFN0LwBf"),sQuery(id+"F0.wireOp",EDGE,"cmr94KfM-78bh-h436-o3Y6-E5B6DGNtIqfJ")])]});
            var Q11;
            Q11=makeQuery(id+"F3.opRevolve","SWEPT_EDGE",EDGE,{"disambiguationData":[OSD([sQuery(id+"F0.wireOp",EDGE,"cmr94KfM-78bh-h436-o3Y6-E5B6DGNtIqfJ"),sQuery(id+"F0.wireOp",EDGE,"ut3q9B5h-MosH-EnmA-Wy3q-ChUi5hh3IWyW")])]});
            var Q12;
            Q12=makeQuery(id+"F3.opRevolve","SWEPT_EDGE",EDGE,{"disambiguationData":[OSD([sQuery(id+"F0.wireOp",EDGE,"E25"),sQuery(id+"F0.wireOp",EDGE,"E26")])]});
            var Q13;
            Q13=makeQuery(id+"F4.opRevolve","SWEPT_EDGE",EDGE,{"disambiguationData":[OSD([sQuery(id+"F0.wireOp",EDGE,"E51.MirrorCS"),sQuery(id+"F0.wireOp",EDGE,"E52.MirrorCS")])]});
            var Q14;
            Q14=makeQuery(id+"F4.opRevolve","SWEPT_EDGE",EDGE,{"disambiguationData":[OSD([sQuery(id+"F0.wireOp",EDGE,"E44"),sQuery(id+"F0.wireOp",EDGE,"E43")])]});
            chamfer(context, id + "F13", {"entities" : qUnion([Q0, Q1, Q2, Q3, Q4, Q5, Q6, Q7, Q8, Q9, Q10, Q11, Q12, Q13, Q14]), "width" : 0.5 * mm, "tangentPropagation" : true});
        }
        {
            var Q0;
            {var subQ0=sQuery(id+"F6.wireOp",EDGE,"E84");Q0=makeQuery(id+"F8.opPattern","COPY",EDGE,{"derivedFrom":makeQuery(id+"F7.opExtrude","CAP_EDGE",EDGE,{"disambiguationData":[OSD([subQ0]),TDD([makeQuery(id+"F6.imprint","IMPRINT",EDGE,{"disambiguationData":[TD([[makeQuery(id+"F6.imprint","INTERSECT",VERTEX,{"disambiguationData":[OD(1.0)],"derivedFrom":[sQuery(id+"F6.wireOp",EDGE,"E83"),subQ0]}),-1.0]])],"derivedFrom":subQ0})])],"isStart":false}),"instanceName":"1"});}
            var Q1;
            {var subQ0=sQuery(id+"F6.wireOp",EDGE,"E84");var subQ1=sQuery(id+"F6.wireOp",EDGE,"E83");var subQ4=sQuery(id+"F0.wireOp",EDGE,"E6");var subQ5=sQuery(id+"F0.wireOp",EDGE,"E5");Q1=makeQuery(id+"F10.opBoolean","SPLIT",EDGE,{"disambiguationData":[TD([makeQuery(id+"F7.opExtrude","SWEPT_FACE",FACE,{"disambiguationData":[OSD([subQ0]),TDD([makeQuery(id+"F6.imprint","IMPRINT",EDGE,{"disambiguationData":[TD([[makeQuery(id+"F6.imprint","INTERSECT",VERTEX,{"disambiguationData":[OD(0.0)],"derivedFrom":[subQ1,subQ0]}),1.0]])],"derivedFrom":subQ0})])]})])],"derivedFrom":makeQuery(id+"F9.opRevolve","SWEPT_EDGE",EDGE,{"disambiguationData":[OSD([subQ5,subQ4,sQuery(id+"F0.wireOp",EDGE,"E15")])]})});}
            var Q2;
            Q2=makeQuery(id+"F8.opPattern","COPY",EDGE,{"derivedFrom":makeQuery(id+"F7.opExtrude","CAP_EDGE",EDGE,{"disambiguationData":[OSD([sQuery(id+"F6.wireOp",EDGE,"E83")])],"isStart":false}),"instanceName":"1"});
            var Q3;
            {var subQ0=sQuery(id+"F6.wireOp",EDGE,"E84");Q3=makeQuery(id+"F8.opPattern","COPY",EDGE,{"derivedFrom":makeQuery(id+"F7.opExtrude","CAP_EDGE",EDGE,{"disambiguationData":[OSD([subQ0]),TDD([makeQuery(id+"F6.imprint","IMPRINT",EDGE,{"disambiguationData":[TD([[makeQuery(id+"F6.imprint","INTERSECT",VERTEX,{"disambiguationData":[OD(0.0)],"derivedFrom":[sQuery(id+"F6.wireOp",EDGE,"E83"),subQ0]}),1.0]])],"derivedFrom":subQ0})])],"isStart":false}),"instanceName":"1"});}
            var Q4;
            {var subQ1=sQuery(id+"F6.wireOp",EDGE,"E84");var subQ2=sQuery(id+"F6.wireOp",EDGE,"E83");var subQ4=sQuery(id+"F0.wireOp",EDGE,"E5");var subQ5=sQuery(id+"F0.wireOp",EDGE,"E6");Q4=makeQuery(id+"F10.opBoolean","SPLIT",EDGE,{"disambiguationData":[TD([makeQuery(id+"F8.opPattern","COPY",FACE,{"derivedFrom":makeQuery(id+"F7.opExtrude","SWEPT_FACE",FACE,{"disambiguationData":[OSD([subQ1]),TDD([makeQuery(id+"F6.imprint","IMPRINT",EDGE,{"disambiguationData":[TD([[makeQuery(id+"F6.imprint","INTERSECT",VERTEX,{"disambiguationData":[OD(0.0)],"derivedFrom":[subQ2,subQ1]}),1.0]])],"derivedFrom":subQ1})])]}),"instanceName":"1"})])],"derivedFrom":makeQuery(id+"F9.opRevolve","SWEPT_EDGE",EDGE,{"disambiguationData":[OSD([subQ4,subQ5,sQuery(id+"F0.wireOp",EDGE,"E15")])]})});}
            var Q5;
            {var subQ0=sQuery(id+"F6.wireOp",EDGE,"E84");Q5=makeQuery(id+"F8.opPattern","COPY",EDGE,{"derivedFrom":makeQuery(id+"F7.opExtrude","CAP_EDGE",EDGE,{"disambiguationData":[OSD([subQ0]),TDD([makeQuery(id+"F6.imprint","IMPRINT",EDGE,{"disambiguationData":[TD([[makeQuery(id+"F6.imprint","INTERSECT",VERTEX,{"disambiguationData":[OD(1.0)],"derivedFrom":[sQuery(id+"F6.wireOp",EDGE,"E83"),subQ0]}),-1.0]])],"derivedFrom":subQ0})])],"isStart":false}),"instanceName":"2"});}
            var Q6;
            Q6=makeQuery(id+"F8.opPattern","COPY",EDGE,{"derivedFrom":makeQuery(id+"F7.opExtrude","CAP_EDGE",EDGE,{"disambiguationData":[OSD([sQuery(id+"F6.wireOp",EDGE,"E83")])],"isStart":false}),"instanceName":"2"});
            var Q7;
            {var subQ0=sQuery(id+"F6.wireOp",EDGE,"E84");Q7=makeQuery(id+"F8.opPattern","COPY",EDGE,{"derivedFrom":makeQuery(id+"F7.opExtrude","CAP_EDGE",EDGE,{"disambiguationData":[OSD([subQ0]),TDD([makeQuery(id+"F6.imprint","IMPRINT",EDGE,{"disambiguationData":[TD([[makeQuery(id+"F6.imprint","INTERSECT",VERTEX,{"disambiguationData":[OD(0.0)],"derivedFrom":[sQuery(id+"F6.wireOp",EDGE,"E83"),subQ0]}),1.0]])],"derivedFrom":subQ0})])],"isStart":false}),"instanceName":"2"});}
            var Q8;
            {var subQ0=sQuery(id+"F6.wireOp",EDGE,"E84");Q8=makeQuery(id+"F7.opExtrude","CAP_EDGE",EDGE,{"disambiguationData":[OSD([subQ0]),TDD([makeQuery(id+"F6.imprint","IMPRINT",EDGE,{"disambiguationData":[TD([[makeQuery(id+"F6.imprint","INTERSECT",VERTEX,{"disambiguationData":[OD(1.0)],"derivedFrom":[sQuery(id+"F6.wireOp",EDGE,"E83"),subQ0]}),-1.0]])],"derivedFrom":subQ0})])],"isStart":false});}
            var Q9;
            Q9=makeQuery(id+"F7.opExtrude","CAP_EDGE",EDGE,{"disambiguationData":[OSD([sQuery(id+"F6.wireOp",EDGE,"E83")])],"isStart":false});
            var Q10;
            {var subQ0=sQuery(id+"F6.wireOp",EDGE,"E84");Q10=makeQuery(id+"F7.opExtrude","CAP_EDGE",EDGE,{"disambiguationData":[OSD([subQ0]),TDD([makeQuery(id+"F6.imprint","IMPRINT",EDGE,{"disambiguationData":[TD([[makeQuery(id+"F6.imprint","INTERSECT",VERTEX,{"disambiguationData":[OD(0.0)],"derivedFrom":[sQuery(id+"F6.wireOp",EDGE,"E83"),subQ0]}),1.0]])],"derivedFrom":subQ0})])],"isStart":false});}
            var Q11;
            {var subQ0=sQuery(id+"F6.wireOp",EDGE,"E84");Q11=makeQuery(id+"F7.opExtrude","CAP_EDGE",EDGE,{"disambiguationData":[OSD([subQ0]),TDD([makeQuery(id+"F6.imprint","IMPRINT",EDGE,{"disambiguationData":[TD([[makeQuery(id+"F6.imprint","INTERSECT",VERTEX,{"disambiguationData":[OD(0.0)],"derivedFrom":[sQuery(id+"F6.wireOp",EDGE,"E83"),subQ0]}),1.0]])],"derivedFrom":subQ0})])],"isStart":true});}
            var Q12;
            Q12=makeQuery(id+"F7.opExtrude","CAP_EDGE",EDGE,{"disambiguationData":[OSD([sQuery(id+"F6.wireOp",EDGE,"E83")])],"isStart":true});
            var Q13;
            {var subQ0=sQuery(id+"F6.wireOp",EDGE,"E84");Q13=makeQuery(id+"F8.opPattern","COPY",EDGE,{"derivedFrom":makeQuery(id+"F7.opExtrude","CAP_EDGE",EDGE,{"disambiguationData":[OSD([subQ0]),TDD([makeQuery(id+"F6.imprint","IMPRINT",EDGE,{"disambiguationData":[TD([[makeQuery(id+"F6.imprint","INTERSECT",VERTEX,{"disambiguationData":[OD(0.0)],"derivedFrom":[sQuery(id+"F6.wireOp",EDGE,"E83"),subQ0]}),1.0]])],"derivedFrom":subQ0})])],"isStart":true}),"instanceName":"2"});}
            var Q14;
            Q14=makeQuery(id+"F8.opPattern","COPY",EDGE,{"derivedFrom":makeQuery(id+"F7.opExtrude","CAP_EDGE",EDGE,{"disambiguationData":[OSD([sQuery(id+"F6.wireOp",EDGE,"E83")])],"isStart":true}),"instanceName":"2"});
            var Q15;
            {var subQ0=sQuery(id+"F6.wireOp",EDGE,"E84");Q15=makeQuery(id+"F8.opPattern","COPY",EDGE,{"derivedFrom":makeQuery(id+"F7.opExtrude","CAP_EDGE",EDGE,{"disambiguationData":[OSD([subQ0]),TDD([makeQuery(id+"F6.imprint","IMPRINT",EDGE,{"disambiguationData":[TD([[makeQuery(id+"F6.imprint","INTERSECT",VERTEX,{"disambiguationData":[OD(1.0)],"derivedFrom":[sQuery(id+"F6.wireOp",EDGE,"E83"),subQ0]}),-1.0]])],"derivedFrom":subQ0})])],"isStart":true}),"instanceName":"2"});}
            var Q16;
            {var subQ1=sQuery(id+"F6.wireOp",EDGE,"E84");var subQ2=sQuery(id+"F6.wireOp",EDGE,"E83");var subQ4=sQuery(id+"F0.wireOp",EDGE,"E30.MirrorCS");var subQ5=sQuery(id+"F0.wireOp",EDGE,"E40.MirrorCS");Q16=makeQuery(id+"F10.opBoolean","SPLIT",EDGE,{"disambiguationData":[TD([makeQuery(id+"F8.opPattern","COPY",FACE,{"derivedFrom":makeQuery(id+"F7.opExtrude","SWEPT_FACE",FACE,{"disambiguationData":[OSD([subQ1]),TDD([makeQuery(id+"F6.imprint","IMPRINT",EDGE,{"disambiguationData":[TD([[makeQuery(id+"F6.imprint","INTERSECT",VERTEX,{"disambiguationData":[OD(0.0)],"derivedFrom":[subQ2,subQ1]}),1.0]])],"derivedFrom":subQ1})])]}),"instanceName":"1"})])],"derivedFrom":makeQuery(id+"F9.opRevolve","SWEPT_EDGE",EDGE,{"disambiguationData":[OSD([subQ4,sQuery(id+"F0.wireOp",EDGE,"E35.MirrorCS"),subQ5])]})});}
            var Q17;
            {var subQ0=sQuery(id+"F6.wireOp",EDGE,"E84");Q17=makeQuery(id+"F8.opPattern","COPY",EDGE,{"derivedFrom":makeQuery(id+"F7.opExtrude","CAP_EDGE",EDGE,{"disambiguationData":[OSD([subQ0]),TDD([makeQuery(id+"F6.imprint","IMPRINT",EDGE,{"disambiguationData":[TD([[makeQuery(id+"F6.imprint","INTERSECT",VERTEX,{"disambiguationData":[OD(0.0)],"derivedFrom":[sQuery(id+"F6.wireOp",EDGE,"E83"),subQ0]}),1.0]])],"derivedFrom":subQ0})])],"isStart":true}),"instanceName":"1"});}
            var Q18;
            Q18=makeQuery(id+"F8.opPattern","COPY",EDGE,{"derivedFrom":makeQuery(id+"F7.opExtrude","CAP_EDGE",EDGE,{"disambiguationData":[OSD([sQuery(id+"F6.wireOp",EDGE,"E83")])],"isStart":true}),"instanceName":"1"});
            var Q19;
            {var subQ0=sQuery(id+"F6.wireOp",EDGE,"E84");Q19=makeQuery(id+"F8.opPattern","COPY",EDGE,{"derivedFrom":makeQuery(id+"F7.opExtrude","CAP_EDGE",EDGE,{"disambiguationData":[OSD([subQ0]),TDD([makeQuery(id+"F6.imprint","IMPRINT",EDGE,{"disambiguationData":[TD([[makeQuery(id+"F6.imprint","INTERSECT",VERTEX,{"disambiguationData":[OD(1.0)],"derivedFrom":[sQuery(id+"F6.wireOp",EDGE,"E83"),subQ0]}),-1.0]])],"derivedFrom":subQ0})])],"isStart":true}),"instanceName":"1"});}
            var Q20;
            {var subQ0=sQuery(id+"F6.wireOp",EDGE,"E84");var subQ1=sQuery(id+"F6.wireOp",EDGE,"E83");var subQ4=sQuery(id+"F0.wireOp",EDGE,"E30.MirrorCS");var subQ5=sQuery(id+"F0.wireOp",EDGE,"E40.MirrorCS");Q20=makeQuery(id+"F10.opBoolean","SPLIT",EDGE,{"disambiguationData":[TD([makeQuery(id+"F7.opExtrude","SWEPT_FACE",FACE,{"disambiguationData":[OSD([subQ0]),TDD([makeQuery(id+"F6.imprint","IMPRINT",EDGE,{"disambiguationData":[TD([[makeQuery(id+"F6.imprint","INTERSECT",VERTEX,{"disambiguationData":[OD(0.0)],"derivedFrom":[subQ1,subQ0]}),1.0]])],"derivedFrom":subQ0})])]})])],"derivedFrom":makeQuery(id+"F9.opRevolve","SWEPT_EDGE",EDGE,{"disambiguationData":[OSD([subQ4,sQuery(id+"F0.wireOp",EDGE,"E35.MirrorCS"),subQ5])]})});}
            var Q21;
            {var subQ0=sQuery(id+"F6.wireOp",EDGE,"E84");Q21=makeQuery(id+"F7.opExtrude","CAP_EDGE",EDGE,{"disambiguationData":[OSD([subQ0]),TDD([makeQuery(id+"F6.imprint","IMPRINT",EDGE,{"disambiguationData":[TD([[makeQuery(id+"F6.imprint","INTERSECT",VERTEX,{"disambiguationData":[OD(1.0)],"derivedFrom":[sQuery(id+"F6.wireOp",EDGE,"E83"),subQ0]}),-1.0]])],"derivedFrom":subQ0})])],"isStart":true});}
            var Q22;
            {var subQ1=sQuery(id+"F6.wireOp",EDGE,"E84");var subQ2=sQuery(id+"F6.wireOp",EDGE,"E83");var subQ4=sQuery(id+"F0.wireOp",EDGE,"E30.MirrorCS");var subQ5=sQuery(id+"F0.wireOp",EDGE,"E40.MirrorCS");Q22=makeQuery(id+"F10.opBoolean","SPLIT",EDGE,{"disambiguationData":[TD([makeQuery(id+"F7.opExtrude","SWEPT_FACE",FACE,{"disambiguationData":[OSD([subQ1]),TDD([makeQuery(id+"F6.imprint","IMPRINT",EDGE,{"disambiguationData":[TD([[makeQuery(id+"F6.imprint","INTERSECT",VERTEX,{"disambiguationData":[OD(1.0)],"derivedFrom":[subQ2,subQ1]}),-1.0]])],"derivedFrom":subQ1})])]})])],"derivedFrom":makeQuery(id+"F9.opRevolve","SWEPT_EDGE",EDGE,{"disambiguationData":[OSD([subQ4,sQuery(id+"F0.wireOp",EDGE,"E35.MirrorCS"),subQ5])]})});}
            var Q23;
            {var subQ1=sQuery(id+"F6.wireOp",EDGE,"E84");var subQ2=sQuery(id+"F6.wireOp",EDGE,"E83");var subQ4=sQuery(id+"F0.wireOp",EDGE,"E5");var subQ5=sQuery(id+"F0.wireOp",EDGE,"E6");Q23=makeQuery(id+"F10.opBoolean","SPLIT",EDGE,{"disambiguationData":[TD([makeQuery(id+"F7.opExtrude","SWEPT_FACE",FACE,{"disambiguationData":[OSD([subQ1]),TDD([makeQuery(id+"F6.imprint","IMPRINT",EDGE,{"disambiguationData":[TD([[makeQuery(id+"F6.imprint","INTERSECT",VERTEX,{"disambiguationData":[OD(1.0)],"derivedFrom":[subQ2,subQ1]}),-1.0]])],"derivedFrom":subQ1})])]})])],"derivedFrom":makeQuery(id+"F9.opRevolve","SWEPT_EDGE",EDGE,{"disambiguationData":[OSD([subQ4,subQ5,sQuery(id+"F0.wireOp",EDGE,"E15")])]})});}
            chamfer(context, id + "F14", {"entities" : qUnion([Q0, Q1, Q2, Q3, Q4, Q5, Q6, Q7, Q8, Q9, Q10, Q11, Q12, Q13, Q14, Q15, Q16, Q17, Q18, Q19, Q20, Q21, Q22, Q23]), "width" : 1.5 * mm, "tangentPropagation" : true});
        }
        {
            var Q0;
            Q0=makeQuery(id+"F3.opRevolve","SWEPT_EDGE",EDGE,{"disambiguationData":[OSD([sQuery(id+"F0.wireOp",EDGE,"E18"),sQuery(id+"F0.wireOp",EDGE,"E63")])]});
            var Q1;
            {var subQ0=sQuery(id+"F0.wireOp",EDGE,"E25");Q1=makeQuery(id+"F13.opChamfer","BLEND_EDGE",EDGE,{"blendedFrom":[makeQuery(id+"F3.opRevolve","SWEPT_EDGE",EDGE,{"disambiguationData":[OSD([subQ0,sQuery(id+"F0.wireOp",EDGE,"E26")])]}),makeQuery(id+"F3.opRevolve","SWEPT_FACE",FACE,{"disambiguationData":[OSD([sQuery(id+"F0.wireOp",EDGE,"E17"),subQ0])]})],"blendedInto":[makeQuery(id+"F3.opRevolve","SWEPT_FACE",FACE,{"disambiguationData":[OSD([sQuery(id+"F0.wireOp",EDGE,"E17"),subQ0])]})]});}
            var Q2;
            Q2=makeQuery(id+"F3.opRevolve","SWEPT_EDGE",EDGE,{"disambiguationData":[OSD([sQuery(id+"F0.wireOp",EDGE,"E17"),sQuery(id+"F0.wireOp",EDGE,"E24"),sQuery(id+"F0.wireOp",EDGE,"E49")])]});
            var Q3;
            {var subQ0=sQuery(id+"F0.wireOp",EDGE,"E52.MirrorCS");Q3=makeQuery(id+"F13.opChamfer","BLEND_EDGE",EDGE,{"blendedFrom":[makeQuery(id+"F4.opRevolve","SWEPT_EDGE",EDGE,{"disambiguationData":[OSD([sQuery(id+"F0.wireOp",EDGE,"E51.MirrorCS"),subQ0])]}),makeQuery(id+"F4.opRevolve","SWEPT_FACE",FACE,{"disambiguationData":[OSD([sQuery(id+"F0.wireOp",EDGE,"E50.MirrorCS"),subQ0])]})],"blendedInto":[makeQuery(id+"F4.opRevolve","SWEPT_FACE",FACE,{"disambiguationData":[OSD([sQuery(id+"F0.wireOp",EDGE,"E50.MirrorCS"),subQ0])]})]});}
            var Q4;
            Q4=makeQuery(id+"F4.opRevolve","SWEPT_EDGE",EDGE,{"disambiguationData":[OSD([sQuery(id+"F0.wireOp",EDGE,"E50.MirrorCS"),sQuery(id+"F0.wireOp",EDGE,"E54.MirrorCS"),sQuery(id+"F0.wireOp",EDGE,"E58.MirrorCS")])]});
            var Q5;
            Q5=makeQuery(id+"F4.opRevolve","SWEPT_EDGE",EDGE,{"disambiguationData":[OSD([sQuery(id+"F0.wireOp",EDGE,"E53.MirrorCS"),sQuery(id+"F0.wireOp",EDGE,"E66.MirrorCS")])]});
            var Q6;
            Q6=makeQuery(id+"F4.opRevolve","SWEPT_EDGE",EDGE,{"disambiguationData":[OSD([sQuery(id+"F0.wireOp",EDGE,"E53.MirrorCS"),sQuery(id+"F0.wireOp",EDGE,"E55.MirrorCS")])]});
            var Q7;
            Q7=makeQuery(id+"F3.opRevolve","SWEPT_EDGE",EDGE,{"disambiguationData":[OSD([sQuery(id+"F0.wireOp",EDGE,"E18"),sQuery(id+"F0.wireOp",EDGE,"E27")])]});
            fillet(context, id + "F15", {"entities" : qUnion([Q0, Q1, Q2, Q3, Q4, Q5, Q6, Q7]), "radius" : 1 * mm, "tangentPropagation" : true, "allowEdgeOverflow" : false});
        }
    });
